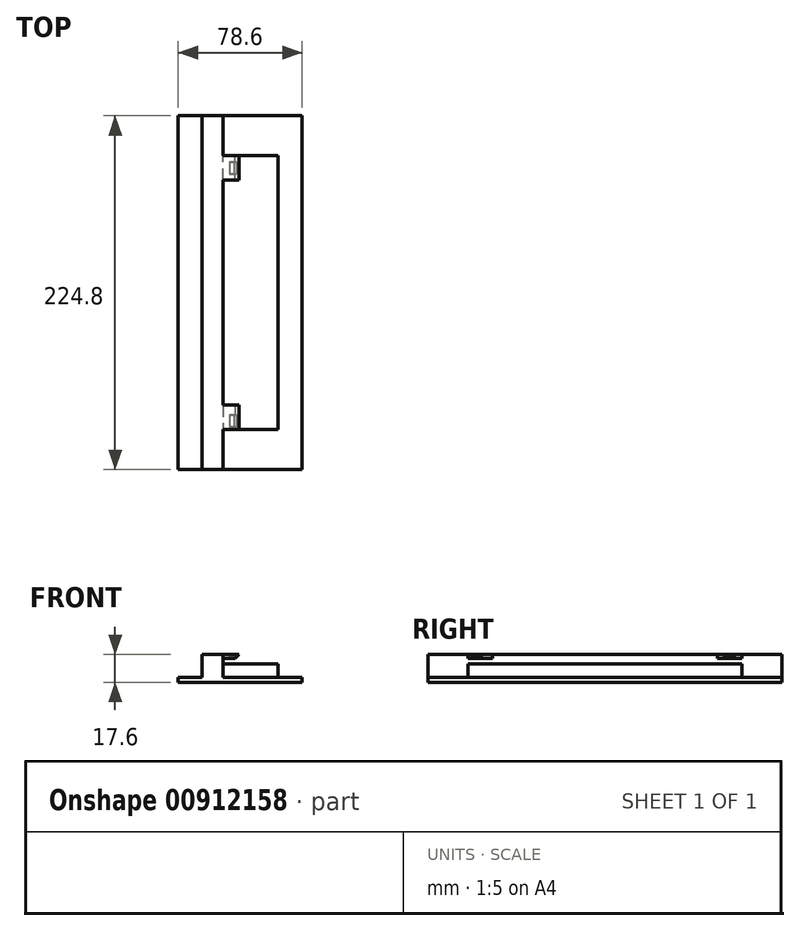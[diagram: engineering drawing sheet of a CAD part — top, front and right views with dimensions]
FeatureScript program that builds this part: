
annotation { "Feature Type Name" : "Feature", "Feature Type Description" : "" }
export const myFeature = defineFeature(function(context is Context, id is Id, definition is map)
    precondition{}
    {
        {
            var Q0;
            Q0=qCreatedBy(makeId("Top.planeOp"),FACE);
            var sketch = newSketch(context, id + "F0", { "sketchPlane" : qUnion([Q0])});
            skLineSegment(sketch, "E0.bottom", {"start": v(-39.3, 112.4) * mm, "end": v(39.3, 112.4) * mm});
            skLineSegment(sketch, "E0.top", {"start": v(-39.3, -112.4) * mm, "end": v(39.3, -112.4) * mm});
            skLineSegment(sketch, "E0.left", {"start": v(-39.3, 112.4) * mm, "end": v(-39.3, -112.4) * mm});
            skLineSegment(sketch, "E0.right", {"start": v(39.3, 112.4) * mm, "end": v(39.3, -112.4) * mm});
            skPoint(sketch, "E0.middle", {"position": v(0, 0) * mm});
            skSolve(sketch);
        }
        {
            var Q0;
            Q0 = qSketchRegion(id + "F0", true);
            extrude(context, id + "F1", {"entities" : qUnion([Q0]), "depth" : 3 * mm, "offsetDistance" : 25 * mm});
        }
        {
            var Q0;
            Q0=makeQuery(id+"F1.opExtrude","SWEPT_FACE",FACE,{"disambiguationData":[OSD([sQuery(id+"F0.wireOp",EDGE,"E0.top")])]});
            var sketch = newSketch(context, id + "F2", { "sketchPlane" : qUnion([Q0])});
            skPoint(sketch, "E1", {"position": v(-24.3, 3) * mm});
            skPoint(sketch, "E2", {"position": v(-10.9, 17.6) * mm});
            skLineSegment(sketch, "E3.bottom", {"start": v(-24.3, 3) * mm, "end": v(-10.9, 3) * mm});
            skLineSegment(sketch, "E3.top", {"start": v(-24.3, 17.6) * mm, "end": v(-10.9, 17.6) * mm});
            skLineSegment(sketch, "E3.left", {"start": v(-24.3, 3) * mm, "end": v(-24.3, 17.6) * mm});
            skLineSegment(sketch, "E3.right", {"start": v(-10.9, 3) * mm, "end": v(-10.9, 17.6) * mm});
            skSolve(sketch);
        }
        {
            var Q0;
            Q0 = qSketchRegion(id + "F2", true);
            var Q1;
            Q1=makeQuery(id+"F1.opExtrude","SWEPT_FACE",FACE,{"disambiguationData":[OSD([sQuery(id+"F0.wireOp",EDGE,"E0.bottom")])]});
            extrude(context, id + "F3", {"entities" : qUnion([Q0]), "operationType" : NewBodyOperationType.ADD, "endBound" : BoundingType.UP_TO_SURFACE, "oppositeDirection" : true, "depth" : 25 * mm, "endBoundEntityFace" : qUnion([Q1]), "offsetDistance" : 25 * mm});
        }
        {
            var Q0;
            Q0=makeQuery(id+"F3.boolean.opBoolean","MERGE",FACE,{"derivedFrom":[makeQuery(id+"F1.opExtrude","SWEPT_FACE",FACE,{"disambiguationData":[OSD([sQuery(id+"F0.wireOp",EDGE,"E0.top")])]}),makeQuery(id+"F3.opExtrude","CAP_FACE",FACE,{"disambiguationData":[OSD([sQuery(id+"F2.wireOp",EDGE,"E3.bottom"),sQuery(id+"F2.wireOp",EDGE,"E3.top"),sQuery(id+"F2.wireOp",EDGE,"E3.left"),sQuery(id+"F2.wireOp",EDGE,"E3.right")])],"isStart":true})]});
            cPlane(context, id + "F4", {"entities" : qUnion([Q0]), "cplaneType" : CPlaneType.OFFSET, "offset" : 25.5 * mm, "oppositeDirection" : true, "width" : 150 * mm, "height" : 150 * mm});
        }
        {
            var Q0;
            Q0=qCreatedBy(id+"F4.planeOp",FACE);
            var sketch = newSketch(context, id + "F5", { "sketchPlane" : qUnion([Q0])});
            skPoint(sketch, "E4", {"position": v(-10.9, 3) * mm});
            skLineSegment(sketch, "E5", {"start": v(-10.9, 3) * mm, "end": v(24.2, 3) * mm});
            skLineSegment(sketch, "E6", {"start": v(24.2, 3) * mm, "end": v(24.2, 11.8) * mm});
            skLineSegment(sketch, "E7", {"start": v(24.2, 11.8) * mm, "end": v(-10.9, 11.8) * mm});
            skLineSegment(sketch, "E8", {"start": v(-10.9, 11.8) * mm, "end": v(-10.9, 3) * mm});
            skSolve(sketch);
        }
        {
            var Q0;
            Q0 = qSketchRegion(id + "F5", true);
            extrude(context, id + "F6", {"entities" : qUnion([Q0]), "operationType" : NewBodyOperationType.ADD, "oppositeDirection" : true, "depth" : 174 * mm, "offsetDistance" : 25 * mm});
        }
        {
            var Q0;
            Q0=qCreatedBy(id+"F4.planeOp",FACE);
            var sketch = newSketch(context, id + "F7", { "sketchPlane" : qUnion([Q0])});
            skPoint(sketch, "E9", {"position": v(-10.9, 15.2) * mm});
            skLineSegment(sketch, "E10", {"start": v(-10.9, 15.2) * mm, "end": v(-10.9, 17.6) * mm});
            skLineSegment(sketch, "E11", {"start": v(-10.9, 17.6) * mm, "end": v(-0.6, 17.6) * mm});
            skLineSegment(sketch, "E12", {"start": v(-0.6, 17.6) * mm, "end": v(-3.2, 15.2) * mm});
            skLineSegment(sketch, "E13", {"start": v(-3.2, 15.2) * mm, "end": v(-10.9, 15.2) * mm});
            skSolve(sketch);
        }
        {
            var Q0;
            Q0=makeQuery(id+"F7.imprint","IMPRINT",FACE,{"disambiguationData":[TD([[makeQuery(id+"F7.imprint","IMPRINT",EDGE,{"derivedFrom":sQuery(id+"F7.wireOp",EDGE,"E10")}),-1.0]])]});
            var Q1;
            Q1=sQuery(id+"F7.wireOp",EDGE,"E12");
            extrude(context, id + "F8", {"entities" : qUnion([Q0]), "operationType" : NewBodyOperationType.ADD, "surfaceEntities" : qUnion([Q1]), "oppositeDirection" : true, "depth" : 15.5 * mm, "offsetDistance" : 25 * mm});
        }
        {
            var Q0;
            Q0=makeQuery(id+"F1.opExtrude","SWEPT_BODY",BODY,{"disambiguationData":[OSD([sQuery(id+"F0.wireOp",EDGE,"E0.bottom"),sQuery(id+"F0.wireOp",EDGE,"E0.top"),sQuery(id+"F0.wireOp",EDGE,"E0.left"),sQuery(id+"F0.wireOp",EDGE,"E0.right")])]});
            var Q1;
            Q1=qCreatedBy(makeId("Front.planeOp"),FACE);
            mirror(context, id + "F9", {"operationType" : NewBodyOperationType.ADD, "entities" : qUnion([Q0]), "mirrorPlane" : qUnion([Q1])});
        }
        {
            var Q0;
            Q0=makeQuery(id+"F8.opExtrude","CAP_FACE",FACE,{"disambiguationData":[OSD([sQuery(id+"F7.wireOp",EDGE,"E10"),sQuery(id+"F7.wireOp",EDGE,"E11"),sQuery(id+"F7.wireOp",EDGE,"E12"),sQuery(id+"F7.wireOp",EDGE,"E13")])],"isStart":true});
            cPlane(context, id + "F10", {"entities" : qUnion([Q0]), "cplaneType" : CPlaneType.OFFSET, "offset" : 1.7 * mm, "oppositeDirection" : true, "width" : 150 * mm, "height" : 150 * mm});
        }
        {
            var Q0;
            Q0=qCreatedBy(id+"F10.planeOp",FACE);
            var sketch = newSketch(context, id + "F11", { "sketchPlane" : qUnion([Q0])});
            skLineSegment(sketch, "E14", {"start": v(-6.84, 15.2) * mm, "end": v(-6.84, 16.9) * mm});
            skLineSegment(sketch, "E15", {"start": v(-6.84, 16.9) * mm, "end": v(-3.74, 16.9) * mm});
            skLineSegment(sketch, "E16", {"start": v(-3.74, 16.9) * mm, "end": v(-3.74, 15.9) * mm});
            skLineSegment(sketch, "E17", {"start": v(-3.74, 15.9) * mm, "end": v(-2.44, 15.9) * mm});
            skLineSegment(sketch, "E18", {"start": v(-2.44, 15.9) * mm, "end": v(-3.2, 15.2) * mm});
            skLineSegment(sketch, "E19", {"start": v(-3.2, 15.2) * mm, "end": v(-6.84, 15.2) * mm});
            skSolve(sketch);
        }
        {
            var Q0;
            Q0 = qSketchRegion(id + "F11", true);
            extrude(context, id + "F12", {"entities" : qUnion([Q0]), "operationType" : NewBodyOperationType.REMOVE, "oppositeDirection" : true, "depth" : 7.4 * mm, "offsetDistance" : 25 * mm});
        }
        {
            var Q0;
            Q0=makeQuery(id+"F9.opPattern","COPY",FACE,{"derivedFrom":makeQuery(id+"F8.opExtrude","CAP_FACE",FACE,{"disambiguationData":[OSD([sQuery(id+"F7.wireOp",EDGE,"E10"),sQuery(id+"F7.wireOp",EDGE,"E11"),sQuery(id+"F7.wireOp",EDGE,"E12"),sQuery(id+"F7.wireOp",EDGE,"E13")])],"isStart":false}),"instanceName":"1"});
            cPlane(context, id + "F13", {"entities" : qUnion([Q0]), "cplaneType" : CPlaneType.OFFSET, "offset" : 4 * mm, "oppositeDirection" : true, "width" : 150 * mm, "height" : 150 * mm});
        }
        {
            var Q0;
            Q0=qCreatedBy(id+"F13.planeOp",FACE);
            var sketch = newSketch(context, id + "F14", { "sketchPlane" : qUnion([Q0])});
            skLineSegment(sketch, "E20", {"start": v(-6.84, 15.2) * mm, "end": v(-6.84, 16.9) * mm});
            skLineSegment(sketch, "E21", {"start": v(-6.84, 16.9) * mm, "end": v(-3.74, 16.9) * mm});
            skLineSegment(sketch, "E22", {"start": v(-3.74, 16.9) * mm, "end": v(-3.74, 15.9) * mm});
            skLineSegment(sketch, "E23", {"start": v(-3.74, 15.9) * mm, "end": v(-2.44, 15.9) * mm});
            skLineSegment(sketch, "E24", {"start": v(-2.44, 15.9) * mm, "end": v(-3.2, 15.2) * mm});
            skLineSegment(sketch, "E25", {"start": v(-3.2, 15.2) * mm, "end": v(-6.84, 15.2) * mm});
            skSolve(sketch);
        }
        {
            var Q0;
            Q0 = qSketchRegion(id + "F14", true);
            extrude(context, id + "F15", {"entities" : qUnion([Q0]), "operationType" : NewBodyOperationType.REMOVE, "oppositeDirection" : true, "depth" : 7.4 * mm, "offsetDistance" : 25 * mm});
        }
    });
